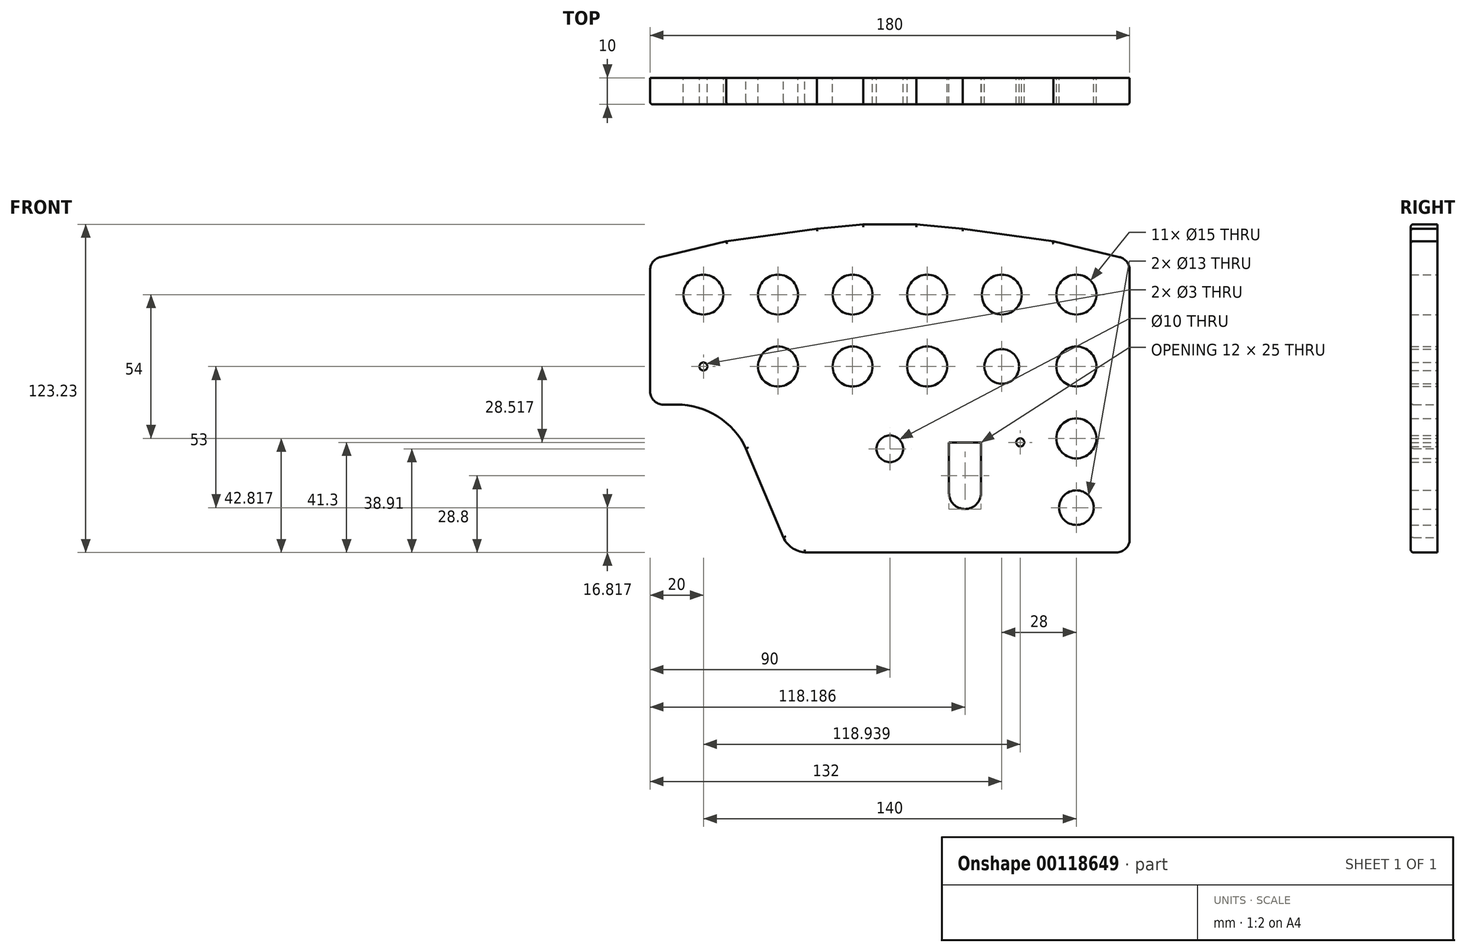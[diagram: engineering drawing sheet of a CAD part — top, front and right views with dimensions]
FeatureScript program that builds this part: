
annotation { "Feature Type Name" : "Feature", "Feature Type Description" : "" }
export const myFeature = defineFeature(function(context is Context, id is Id, definition is map)
    precondition{}
    {
        {
            var Q0;
            Q0=qCreatedBy(makeId("Front.planeOp"),FACE);
            var sketch = newSketch(context, id + "F0", { "sketchPlane" : qUnion([Q0])});
            skLineSegment(sketch, "E0", {"start": v(90, -61.56) * mm, "end": v(-32.02, -61.56) * mm});
            skLineSegment(sketch, "E1", {"start": v(-80.02, -6.06) * mm, "end": v(-90, -6.06) * mm});
            skArc(sketch, "E2", {"start": v(-54.02, -22.56) * mm, "mid": v(-64.6, -10.48) * mm, "end": v(-80.02, -6.06) * mm});
            skArc(sketch, "E3", {"start": v(-40.02, -55.96) * mm, "mid": v(-36.75, -59.8) * mm, "end": v(-32.02, -61.56) * mm});
            skLineSegment(sketch, "E4", {"start": v(-54.02, -22.56) * mm, "end": v(-40.02, -55.96) * mm});
            skLineSegment(sketch, "E5", {"start": v(-90, -6.06) * mm, "end": v(-90, 48.44) * mm});
            skLineSegment(sketch, "E6", {"start": v(-90, 48.44) * mm, "end": v(-61.38, 55.34) * mm});
            skLineSegment(sketch, "E7", {"start": v(61.38, 55.34) * mm, "end": v(90, 48.44) * mm});
            skLineSegment(sketch, "E8", {"start": v(90, 48.44) * mm, "end": v(90, -61.56) * mm});
            skCircle(sketch, "E9", {"center": v(-42, 35.26) * mm, "radius": 7.5 * mm});
            skCircle(sketch, "E10", {"center": v(-42, 8.26) * mm, "radius": 7.5 * mm});
            skCircle(sketch, "E11", {"center": v(-70, 35.26) * mm, "radius": 7.5 * mm});
            skCircle(sketch, "E12", {"center": v(-14, 8.26) * mm, "radius": 7.5 * mm});
            skCircle(sketch, "E13", {"center": v(14, 35.26) * mm, "radius": 7.5 * mm});
            skCircle(sketch, "E14", {"center": v(-14, 35.26) * mm, "radius": 7.5 * mm});
            skCircle(sketch, "E15", {"center": v(14, 8.26) * mm, "radius": 7.5 * mm});
            skCircle(sketch, "E16", {"center": v(42, 35.26) * mm, "radius": 7.5 * mm});
            skCircle(sketch, "E17", {"center": v(70, 35.26) * mm, "radius": 7.5 * mm});
            skCircle(sketch, "E18", {"center": v(70, 8.26) * mm, "radius": 7.5 * mm});
            skCircle(sketch, "E19", {"center": v(70, -18.74) * mm, "radius": 7.5 * mm});
            skCircle(sketch, "E20", {"center": v(42, 8.26) * mm, "radius": 6.5 * mm});
            skCircle(sketch, "E21", {"center": v(0, -22.65) * mm, "radius": 5 * mm});
            skCircle(sketch, "E22", {"center": v(70, -44.74) * mm, "radius": 6.5 * mm});
            skCircle(sketch, "E23", {"center": v(48.94, -20.26) * mm, "radius": 1.5 * mm});
            skLineSegment(sketch, "E24.bottom", {"start": v(22.19, -20.26) * mm, "end": v(34.19, -20.26) * mm});
            skLineSegment(sketch, "E24.top", {"start": v(28.19, -45.26) * mm, "end": v(28.19, -45.26) * mm});
            skLineSegment(sketch, "E24.left", {"start": v(22.19, -20.26) * mm, "end": v(22.19, -39.26) * mm});
            skLineSegment(sketch, "E24.right", {"start": v(34.19, -20.26) * mm, "end": v(34.19, -39.26) * mm});
            skLineSegment(sketch, "E25", {"start": v(-61.38, 55.34) * mm, "end": v(-27.4, 60.04) * mm});
            skLineSegment(sketch, "E26", {"start": v(27.4, 60.04) * mm, "end": v(61.38, 55.34) * mm});
            skLineSegment(sketch, "E27", {"start": v(0, 70.54) * mm, "end": v(0, -4.12) * mm, "construction": true});
            skPoint(sketch, "E28.visualSharp", {"position": v(0, 63.83) * mm});
            skLineSegment(sketch, "E29", {"start": v(-14.08, 0) * mm, "end": v(5.41, 0) * mm, "construction": true});
            skPoint(sketch, "E30.visualSharp", {"position": v(22.19, -45.26) * mm});
            skArc(sketch, "E30.filletArc", {"start": v(22.19, -39.26) * mm, "mid": v(23.94, -43.5) * mm, "end": v(28.19, -45.26) * mm});
            skPoint(sketch, "E31.visualSharp", {"position": v(34.19, -45.26) * mm});
            skArc(sketch, "E31.filletArc", {"start": v(28.19, -45.26) * mm, "mid": v(32.43, -43.5) * mm, "end": v(34.19, -39.26) * mm});
            skLineSegment(sketch, "E32", {"start": v(-10, 70.54) * mm, "end": v(-10, 51.48) * mm, "construction": true});
            skLineSegment(sketch, "E33", {"start": v(10, 70.54) * mm, "end": v(10, 51.64) * mm, "construction": true});
            skLineSegment(sketch, "E34", {"start": v(-27.4, 60.04) * mm, "end": v(-10, 61.67) * mm});
            skLineSegment(sketch, "E35", {"start": v(-10, 61.67) * mm, "end": v(10, 61.67) * mm});
            skLineSegment(sketch, "E36", {"start": v(10, 61.67) * mm, "end": v(27.4, 60.04) * mm});
            skCircle(sketch, "E37", {"center": v(-70, 8.26) * mm, "radius": 1.5 * mm});
            skSolve(sketch);
        }
        {
            var Q0;
            Q0=makeQuery(id+"F0.imprint","IMPRINT",FACE,{"disambiguationData":[TD([[makeQuery(id+"F0.imprint","IMPRINT",EDGE,{"derivedFrom":sQuery(id+"F0.wireOp",EDGE,"E0")}),-1.0]])]});
            extrude(context, id + "F1", {"entities" : qUnion([Q0]), "depth" : 10 * mm});
        }
        {
            var Q0;
            Q0=makeQuery(id+"F1.opExtrude","SWEPT_EDGE",EDGE,{"disambiguationData":[OSD([sQuery(id+"F0.wireOp",EDGE,"E5"),sQuery(id+"F0.wireOp",EDGE,"E6")])]});
            var Q1;
            Q1=makeQuery(id+"F1.opExtrude","SWEPT_EDGE",EDGE,{"disambiguationData":[OSD([sQuery(id+"F0.wireOp",EDGE,"E7"),sQuery(id+"F0.wireOp",EDGE,"E8")])]});
            var Q2;
            Q2=makeQuery(id+"F1.opExtrude","SWEPT_EDGE",EDGE,{"disambiguationData":[OSD([sQuery(id+"F0.wireOp",EDGE,"E1"),sQuery(id+"F0.wireOp",EDGE,"E5")])]});
            var Q3;
            Q3=makeQuery(id+"F1.opExtrude","SWEPT_EDGE",EDGE,{"disambiguationData":[OSD([sQuery(id+"F0.wireOp",EDGE,"E0"),sQuery(id+"F0.wireOp",EDGE,"E8")])]});
            fillet(context, id + "F2", {"entities" : qUnion([Q0, Q1, Q2, Q3]), "radius" : 5 * mm, "tangentPropagation" : true, "allowEdgeOverflow" : false});
        }
        {
            var Q0;
            Q0=makeQuery(id+"F1.opExtrude","CAP_EDGE",EDGE,{"disambiguationData":[OSD([sQuery(id+"F0.wireOp",EDGE,"E35")])],"isStart":false});
            var Q1;
            Q1=makeQuery(id+"F1.opExtrude","CAP_EDGE",EDGE,{"disambiguationData":[OSD([sQuery(id+"F0.wireOp",EDGE,"E36")])],"isStart":false});
            var Q2;
            Q2=makeQuery(id+"F1.opExtrude","CAP_EDGE",EDGE,{"disambiguationData":[OSD([sQuery(id+"F0.wireOp",EDGE,"E26")])],"isStart":false});
            var Q3;
            Q3=makeQuery(id+"F1.opExtrude","CAP_EDGE",EDGE,{"disambiguationData":[OSD([sQuery(id+"F0.wireOp",EDGE,"E7")])],"isStart":false});
            var Q4;
            {var subQ0=sQuery(id+"F0.wireOp",EDGE,"E8");var subQ1=sQuery(id+"F0.wireOp",EDGE,"E7");Q4=makeQuery(id+"F2.opFillet","BLEND_EDGE",EDGE,{"blendedFrom":[makeQuery(id+"F1.opExtrude","SWEPT_EDGE",EDGE,{"disambiguationData":[OSD([subQ1,subQ0])]}),makeQuery(id+"F1.opExtrude","CAP_FACE",FACE,{"disambiguationData":[OSD([sQuery(id+"F0.wireOp",EDGE,"E0"),sQuery(id+"F0.wireOp",EDGE,"E1"),sQuery(id+"F0.wireOp",EDGE,"E2"),sQuery(id+"F0.wireOp",EDGE,"E3"),sQuery(id+"F0.wireOp",EDGE,"E4"),sQuery(id+"F0.wireOp",EDGE,"E5"),sQuery(id+"F0.wireOp",EDGE,"E6"),subQ1,subQ0,sQuery(id+"F0.wireOp",EDGE,"E9"),sQuery(id+"F0.wireOp",EDGE,"E10"),sQuery(id+"F0.wireOp",EDGE,"E11"),sQuery(id+"F0.wireOp",EDGE,"E12"),sQuery(id+"F0.wireOp",EDGE,"E13"),sQuery(id+"F0.wireOp",EDGE,"E14"),sQuery(id+"F0.wireOp",EDGE,"E15"),sQuery(id+"F0.wireOp",EDGE,"E16"),sQuery(id+"F0.wireOp",EDGE,"E17"),sQuery(id+"F0.wireOp",EDGE,"E18"),sQuery(id+"F0.wireOp",EDGE,"E19"),sQuery(id+"F0.wireOp",EDGE,"E20"),sQuery(id+"F0.wireOp",EDGE,"E21"),sQuery(id+"F0.wireOp",EDGE,"E22"),sQuery(id+"F0.wireOp",EDGE,"E23"),sQuery(id+"F0.wireOp",EDGE,"E24.bottom"),sQuery(id+"F0.wireOp",EDGE,"E24.left"),sQuery(id+"F0.wireOp",EDGE,"E24.right"),sQuery(id+"F0.wireOp",EDGE,"E25"),sQuery(id+"F0.wireOp",EDGE,"E26"),sQuery(id+"F0.wireOp",EDGE,"E30.filletArc"),sQuery(id+"F0.wireOp",EDGE,"E31.filletArc"),sQuery(id+"F0.wireOp",EDGE,"E34"),sQuery(id+"F0.wireOp",EDGE,"E35"),sQuery(id+"F0.wireOp",EDGE,"E36"),sQuery(id+"F0.wireOp",EDGE,"E37")])],"isStart":false})],"blendedInto":[makeQuery(id+"F1.opExtrude","CAP_FACE",FACE,{"disambiguationData":[OSD([sQuery(id+"F0.wireOp",EDGE,"E0"),sQuery(id+"F0.wireOp",EDGE,"E1"),sQuery(id+"F0.wireOp",EDGE,"E2"),sQuery(id+"F0.wireOp",EDGE,"E3"),sQuery(id+"F0.wireOp",EDGE,"E4"),sQuery(id+"F0.wireOp",EDGE,"E5"),sQuery(id+"F0.wireOp",EDGE,"E6"),subQ1,subQ0,sQuery(id+"F0.wireOp",EDGE,"E9"),sQuery(id+"F0.wireOp",EDGE,"E10"),sQuery(id+"F0.wireOp",EDGE,"E11"),sQuery(id+"F0.wireOp",EDGE,"E12"),sQuery(id+"F0.wireOp",EDGE,"E13"),sQuery(id+"F0.wireOp",EDGE,"E14"),sQuery(id+"F0.wireOp",EDGE,"E15"),sQuery(id+"F0.wireOp",EDGE,"E16"),sQuery(id+"F0.wireOp",EDGE,"E17"),sQuery(id+"F0.wireOp",EDGE,"E18"),sQuery(id+"F0.wireOp",EDGE,"E19"),sQuery(id+"F0.wireOp",EDGE,"E20"),sQuery(id+"F0.wireOp",EDGE,"E21"),sQuery(id+"F0.wireOp",EDGE,"E22"),sQuery(id+"F0.wireOp",EDGE,"E23"),sQuery(id+"F0.wireOp",EDGE,"E24.bottom"),sQuery(id+"F0.wireOp",EDGE,"E24.left"),sQuery(id+"F0.wireOp",EDGE,"E24.right"),sQuery(id+"F0.wireOp",EDGE,"E25"),sQuery(id+"F0.wireOp",EDGE,"E26"),sQuery(id+"F0.wireOp",EDGE,"E30.filletArc"),sQuery(id+"F0.wireOp",EDGE,"E31.filletArc"),sQuery(id+"F0.wireOp",EDGE,"E34"),sQuery(id+"F0.wireOp",EDGE,"E35"),sQuery(id+"F0.wireOp",EDGE,"E36"),sQuery(id+"F0.wireOp",EDGE,"E37")])],"isStart":false})]});}
            var Q5;
            Q5=makeQuery(id+"F1.opExtrude","CAP_EDGE",EDGE,{"disambiguationData":[OSD([sQuery(id+"F0.wireOp",EDGE,"E8")])],"isStart":false});
            var Q6;
            {var subQ0=sQuery(id+"F0.wireOp",EDGE,"E8");var subQ1=sQuery(id+"F0.wireOp",EDGE,"E0");Q6=makeQuery(id+"F2.opFillet","BLEND_EDGE",EDGE,{"blendedFrom":[makeQuery(id+"F1.opExtrude","SWEPT_EDGE",EDGE,{"disambiguationData":[OSD([subQ1,subQ0])]}),makeQuery(id+"F1.opExtrude","CAP_FACE",FACE,{"disambiguationData":[OSD([subQ1,sQuery(id+"F0.wireOp",EDGE,"E1"),sQuery(id+"F0.wireOp",EDGE,"E2"),sQuery(id+"F0.wireOp",EDGE,"E3"),sQuery(id+"F0.wireOp",EDGE,"E4"),sQuery(id+"F0.wireOp",EDGE,"E5"),sQuery(id+"F0.wireOp",EDGE,"E6"),sQuery(id+"F0.wireOp",EDGE,"E7"),subQ0,sQuery(id+"F0.wireOp",EDGE,"E9"),sQuery(id+"F0.wireOp",EDGE,"E10"),sQuery(id+"F0.wireOp",EDGE,"E11"),sQuery(id+"F0.wireOp",EDGE,"E12"),sQuery(id+"F0.wireOp",EDGE,"E13"),sQuery(id+"F0.wireOp",EDGE,"E14"),sQuery(id+"F0.wireOp",EDGE,"E15"),sQuery(id+"F0.wireOp",EDGE,"E16"),sQuery(id+"F0.wireOp",EDGE,"E17"),sQuery(id+"F0.wireOp",EDGE,"E18"),sQuery(id+"F0.wireOp",EDGE,"E19"),sQuery(id+"F0.wireOp",EDGE,"E20"),sQuery(id+"F0.wireOp",EDGE,"E21"),sQuery(id+"F0.wireOp",EDGE,"E22"),sQuery(id+"F0.wireOp",EDGE,"E23"),sQuery(id+"F0.wireOp",EDGE,"E24.bottom"),sQuery(id+"F0.wireOp",EDGE,"E24.left"),sQuery(id+"F0.wireOp",EDGE,"E24.right"),sQuery(id+"F0.wireOp",EDGE,"E25"),sQuery(id+"F0.wireOp",EDGE,"E26"),sQuery(id+"F0.wireOp",EDGE,"E30.filletArc"),sQuery(id+"F0.wireOp",EDGE,"E31.filletArc"),sQuery(id+"F0.wireOp",EDGE,"E34"),sQuery(id+"F0.wireOp",EDGE,"E35"),sQuery(id+"F0.wireOp",EDGE,"E36"),sQuery(id+"F0.wireOp",EDGE,"E37")])],"isStart":false})],"blendedInto":[makeQuery(id+"F1.opExtrude","CAP_FACE",FACE,{"disambiguationData":[OSD([subQ1,sQuery(id+"F0.wireOp",EDGE,"E1"),sQuery(id+"F0.wireOp",EDGE,"E2"),sQuery(id+"F0.wireOp",EDGE,"E3"),sQuery(id+"F0.wireOp",EDGE,"E4"),sQuery(id+"F0.wireOp",EDGE,"E5"),sQuery(id+"F0.wireOp",EDGE,"E6"),sQuery(id+"F0.wireOp",EDGE,"E7"),subQ0,sQuery(id+"F0.wireOp",EDGE,"E9"),sQuery(id+"F0.wireOp",EDGE,"E10"),sQuery(id+"F0.wireOp",EDGE,"E11"),sQuery(id+"F0.wireOp",EDGE,"E12"),sQuery(id+"F0.wireOp",EDGE,"E13"),sQuery(id+"F0.wireOp",EDGE,"E14"),sQuery(id+"F0.wireOp",EDGE,"E15"),sQuery(id+"F0.wireOp",EDGE,"E16"),sQuery(id+"F0.wireOp",EDGE,"E17"),sQuery(id+"F0.wireOp",EDGE,"E18"),sQuery(id+"F0.wireOp",EDGE,"E19"),sQuery(id+"F0.wireOp",EDGE,"E20"),sQuery(id+"F0.wireOp",EDGE,"E21"),sQuery(id+"F0.wireOp",EDGE,"E22"),sQuery(id+"F0.wireOp",EDGE,"E23"),sQuery(id+"F0.wireOp",EDGE,"E24.bottom"),sQuery(id+"F0.wireOp",EDGE,"E24.left"),sQuery(id+"F0.wireOp",EDGE,"E24.right"),sQuery(id+"F0.wireOp",EDGE,"E25"),sQuery(id+"F0.wireOp",EDGE,"E26"),sQuery(id+"F0.wireOp",EDGE,"E30.filletArc"),sQuery(id+"F0.wireOp",EDGE,"E31.filletArc"),sQuery(id+"F0.wireOp",EDGE,"E34"),sQuery(id+"F0.wireOp",EDGE,"E35"),sQuery(id+"F0.wireOp",EDGE,"E36"),sQuery(id+"F0.wireOp",EDGE,"E37")])],"isStart":false})]});}
            var Q7;
            Q7=makeQuery(id+"F1.opExtrude","CAP_EDGE",EDGE,{"disambiguationData":[OSD([sQuery(id+"F0.wireOp",EDGE,"E0")])],"isStart":false});
            var Q8;
            Q8=makeQuery(id+"F1.opExtrude","CAP_EDGE",EDGE,{"disambiguationData":[OSD([sQuery(id+"F0.wireOp",EDGE,"E3")])],"isStart":false});
            var Q9;
            Q9=makeQuery(id+"F1.opExtrude","CAP_EDGE",EDGE,{"disambiguationData":[OSD([sQuery(id+"F0.wireOp",EDGE,"E4")])],"isStart":false});
            var Q10;
            Q10=makeQuery(id+"F1.opExtrude","CAP_EDGE",EDGE,{"disambiguationData":[OSD([sQuery(id+"F0.wireOp",EDGE,"E2")])],"isStart":false});
            var Q11;
            Q11=makeQuery(id+"F1.opExtrude","CAP_EDGE",EDGE,{"disambiguationData":[OSD([sQuery(id+"F0.wireOp",EDGE,"E1")])],"isStart":false});
            var Q12;
            {var subQ0=sQuery(id+"F0.wireOp",EDGE,"E5");var subQ1=sQuery(id+"F0.wireOp",EDGE,"E1");Q12=makeQuery(id+"F2.opFillet","BLEND_EDGE",EDGE,{"blendedFrom":[makeQuery(id+"F1.opExtrude","SWEPT_EDGE",EDGE,{"disambiguationData":[OSD([subQ1,subQ0])]}),makeQuery(id+"F1.opExtrude","CAP_FACE",FACE,{"disambiguationData":[OSD([sQuery(id+"F0.wireOp",EDGE,"E0"),subQ1,sQuery(id+"F0.wireOp",EDGE,"E2"),sQuery(id+"F0.wireOp",EDGE,"E3"),sQuery(id+"F0.wireOp",EDGE,"E4"),subQ0,sQuery(id+"F0.wireOp",EDGE,"E6"),sQuery(id+"F0.wireOp",EDGE,"E7"),sQuery(id+"F0.wireOp",EDGE,"E8"),sQuery(id+"F0.wireOp",EDGE,"E9"),sQuery(id+"F0.wireOp",EDGE,"E10"),sQuery(id+"F0.wireOp",EDGE,"E11"),sQuery(id+"F0.wireOp",EDGE,"E12"),sQuery(id+"F0.wireOp",EDGE,"E13"),sQuery(id+"F0.wireOp",EDGE,"E14"),sQuery(id+"F0.wireOp",EDGE,"E15"),sQuery(id+"F0.wireOp",EDGE,"E16"),sQuery(id+"F0.wireOp",EDGE,"E17"),sQuery(id+"F0.wireOp",EDGE,"E18"),sQuery(id+"F0.wireOp",EDGE,"E19"),sQuery(id+"F0.wireOp",EDGE,"E20"),sQuery(id+"F0.wireOp",EDGE,"E21"),sQuery(id+"F0.wireOp",EDGE,"E22"),sQuery(id+"F0.wireOp",EDGE,"E23"),sQuery(id+"F0.wireOp",EDGE,"E24.bottom"),sQuery(id+"F0.wireOp",EDGE,"E24.left"),sQuery(id+"F0.wireOp",EDGE,"E24.right"),sQuery(id+"F0.wireOp",EDGE,"E25"),sQuery(id+"F0.wireOp",EDGE,"E26"),sQuery(id+"F0.wireOp",EDGE,"E30.filletArc"),sQuery(id+"F0.wireOp",EDGE,"E31.filletArc"),sQuery(id+"F0.wireOp",EDGE,"E34"),sQuery(id+"F0.wireOp",EDGE,"E35"),sQuery(id+"F0.wireOp",EDGE,"E36"),sQuery(id+"F0.wireOp",EDGE,"E37")])],"isStart":false})],"blendedInto":[makeQuery(id+"F1.opExtrude","CAP_FACE",FACE,{"disambiguationData":[OSD([sQuery(id+"F0.wireOp",EDGE,"E0"),subQ1,sQuery(id+"F0.wireOp",EDGE,"E2"),sQuery(id+"F0.wireOp",EDGE,"E3"),sQuery(id+"F0.wireOp",EDGE,"E4"),subQ0,sQuery(id+"F0.wireOp",EDGE,"E6"),sQuery(id+"F0.wireOp",EDGE,"E7"),sQuery(id+"F0.wireOp",EDGE,"E8"),sQuery(id+"F0.wireOp",EDGE,"E9"),sQuery(id+"F0.wireOp",EDGE,"E10"),sQuery(id+"F0.wireOp",EDGE,"E11"),sQuery(id+"F0.wireOp",EDGE,"E12"),sQuery(id+"F0.wireOp",EDGE,"E13"),sQuery(id+"F0.wireOp",EDGE,"E14"),sQuery(id+"F0.wireOp",EDGE,"E15"),sQuery(id+"F0.wireOp",EDGE,"E16"),sQuery(id+"F0.wireOp",EDGE,"E17"),sQuery(id+"F0.wireOp",EDGE,"E18"),sQuery(id+"F0.wireOp",EDGE,"E19"),sQuery(id+"F0.wireOp",EDGE,"E20"),sQuery(id+"F0.wireOp",EDGE,"E21"),sQuery(id+"F0.wireOp",EDGE,"E22"),sQuery(id+"F0.wireOp",EDGE,"E23"),sQuery(id+"F0.wireOp",EDGE,"E24.bottom"),sQuery(id+"F0.wireOp",EDGE,"E24.left"),sQuery(id+"F0.wireOp",EDGE,"E24.right"),sQuery(id+"F0.wireOp",EDGE,"E25"),sQuery(id+"F0.wireOp",EDGE,"E26"),sQuery(id+"F0.wireOp",EDGE,"E30.filletArc"),sQuery(id+"F0.wireOp",EDGE,"E31.filletArc"),sQuery(id+"F0.wireOp",EDGE,"E34"),sQuery(id+"F0.wireOp",EDGE,"E35"),sQuery(id+"F0.wireOp",EDGE,"E36"),sQuery(id+"F0.wireOp",EDGE,"E37")])],"isStart":false})]});}
            var Q13;
            Q13=makeQuery(id+"F1.opExtrude","CAP_EDGE",EDGE,{"disambiguationData":[OSD([sQuery(id+"F0.wireOp",EDGE,"E5")])],"isStart":false});
            var Q14;
            {var subQ0=sQuery(id+"F0.wireOp",EDGE,"E6");var subQ1=sQuery(id+"F0.wireOp",EDGE,"E5");Q14=makeQuery(id+"F2.opFillet","BLEND_EDGE",EDGE,{"blendedFrom":[makeQuery(id+"F1.opExtrude","SWEPT_EDGE",EDGE,{"disambiguationData":[OSD([subQ1,subQ0])]}),makeQuery(id+"F1.opExtrude","CAP_FACE",FACE,{"disambiguationData":[OSD([sQuery(id+"F0.wireOp",EDGE,"E0"),sQuery(id+"F0.wireOp",EDGE,"E1"),sQuery(id+"F0.wireOp",EDGE,"E2"),sQuery(id+"F0.wireOp",EDGE,"E3"),sQuery(id+"F0.wireOp",EDGE,"E4"),subQ1,subQ0,sQuery(id+"F0.wireOp",EDGE,"E7"),sQuery(id+"F0.wireOp",EDGE,"E8"),sQuery(id+"F0.wireOp",EDGE,"E9"),sQuery(id+"F0.wireOp",EDGE,"E10"),sQuery(id+"F0.wireOp",EDGE,"E11"),sQuery(id+"F0.wireOp",EDGE,"E12"),sQuery(id+"F0.wireOp",EDGE,"E13"),sQuery(id+"F0.wireOp",EDGE,"E14"),sQuery(id+"F0.wireOp",EDGE,"E15"),sQuery(id+"F0.wireOp",EDGE,"E16"),sQuery(id+"F0.wireOp",EDGE,"E17"),sQuery(id+"F0.wireOp",EDGE,"E18"),sQuery(id+"F0.wireOp",EDGE,"E19"),sQuery(id+"F0.wireOp",EDGE,"E20"),sQuery(id+"F0.wireOp",EDGE,"E21"),sQuery(id+"F0.wireOp",EDGE,"E22"),sQuery(id+"F0.wireOp",EDGE,"E23"),sQuery(id+"F0.wireOp",EDGE,"E24.bottom"),sQuery(id+"F0.wireOp",EDGE,"E24.left"),sQuery(id+"F0.wireOp",EDGE,"E24.right"),sQuery(id+"F0.wireOp",EDGE,"E25"),sQuery(id+"F0.wireOp",EDGE,"E26"),sQuery(id+"F0.wireOp",EDGE,"E30.filletArc"),sQuery(id+"F0.wireOp",EDGE,"E31.filletArc"),sQuery(id+"F0.wireOp",EDGE,"E34"),sQuery(id+"F0.wireOp",EDGE,"E35"),sQuery(id+"F0.wireOp",EDGE,"E36"),sQuery(id+"F0.wireOp",EDGE,"E37")])],"isStart":false})],"blendedInto":[makeQuery(id+"F1.opExtrude","CAP_FACE",FACE,{"disambiguationData":[OSD([sQuery(id+"F0.wireOp",EDGE,"E0"),sQuery(id+"F0.wireOp",EDGE,"E1"),sQuery(id+"F0.wireOp",EDGE,"E2"),sQuery(id+"F0.wireOp",EDGE,"E3"),sQuery(id+"F0.wireOp",EDGE,"E4"),subQ1,subQ0,sQuery(id+"F0.wireOp",EDGE,"E7"),sQuery(id+"F0.wireOp",EDGE,"E8"),sQuery(id+"F0.wireOp",EDGE,"E9"),sQuery(id+"F0.wireOp",EDGE,"E10"),sQuery(id+"F0.wireOp",EDGE,"E11"),sQuery(id+"F0.wireOp",EDGE,"E12"),sQuery(id+"F0.wireOp",EDGE,"E13"),sQuery(id+"F0.wireOp",EDGE,"E14"),sQuery(id+"F0.wireOp",EDGE,"E15"),sQuery(id+"F0.wireOp",EDGE,"E16"),sQuery(id+"F0.wireOp",EDGE,"E17"),sQuery(id+"F0.wireOp",EDGE,"E18"),sQuery(id+"F0.wireOp",EDGE,"E19"),sQuery(id+"F0.wireOp",EDGE,"E20"),sQuery(id+"F0.wireOp",EDGE,"E21"),sQuery(id+"F0.wireOp",EDGE,"E22"),sQuery(id+"F0.wireOp",EDGE,"E23"),sQuery(id+"F0.wireOp",EDGE,"E24.bottom"),sQuery(id+"F0.wireOp",EDGE,"E24.left"),sQuery(id+"F0.wireOp",EDGE,"E24.right"),sQuery(id+"F0.wireOp",EDGE,"E25"),sQuery(id+"F0.wireOp",EDGE,"E26"),sQuery(id+"F0.wireOp",EDGE,"E30.filletArc"),sQuery(id+"F0.wireOp",EDGE,"E31.filletArc"),sQuery(id+"F0.wireOp",EDGE,"E34"),sQuery(id+"F0.wireOp",EDGE,"E35"),sQuery(id+"F0.wireOp",EDGE,"E36"),sQuery(id+"F0.wireOp",EDGE,"E37")])],"isStart":false})]});}
            var Q15;
            Q15=makeQuery(id+"F1.opExtrude","CAP_EDGE",EDGE,{"disambiguationData":[OSD([sQuery(id+"F0.wireOp",EDGE,"E6")])],"isStart":false});
            var Q16;
            Q16=makeQuery(id+"F1.opExtrude","CAP_EDGE",EDGE,{"disambiguationData":[OSD([sQuery(id+"F0.wireOp",EDGE,"E25")])],"isStart":false});
            var Q17;
            Q17=makeQuery(id+"F1.opExtrude","CAP_EDGE",EDGE,{"disambiguationData":[OSD([sQuery(id+"F0.wireOp",EDGE,"E34")])],"isStart":false});
            fillet(context, id + "F3", {"entities" : qUnion([Q0, Q1, Q2, Q3, Q4, Q5, Q6, Q7, Q8, Q9, Q10, Q11, Q12, Q13, Q14, Q15, Q16, Q17]), "radius" : 1 * mm, "tangentPropagation" : true, "allowEdgeOverflow" : false});
        }
    });
